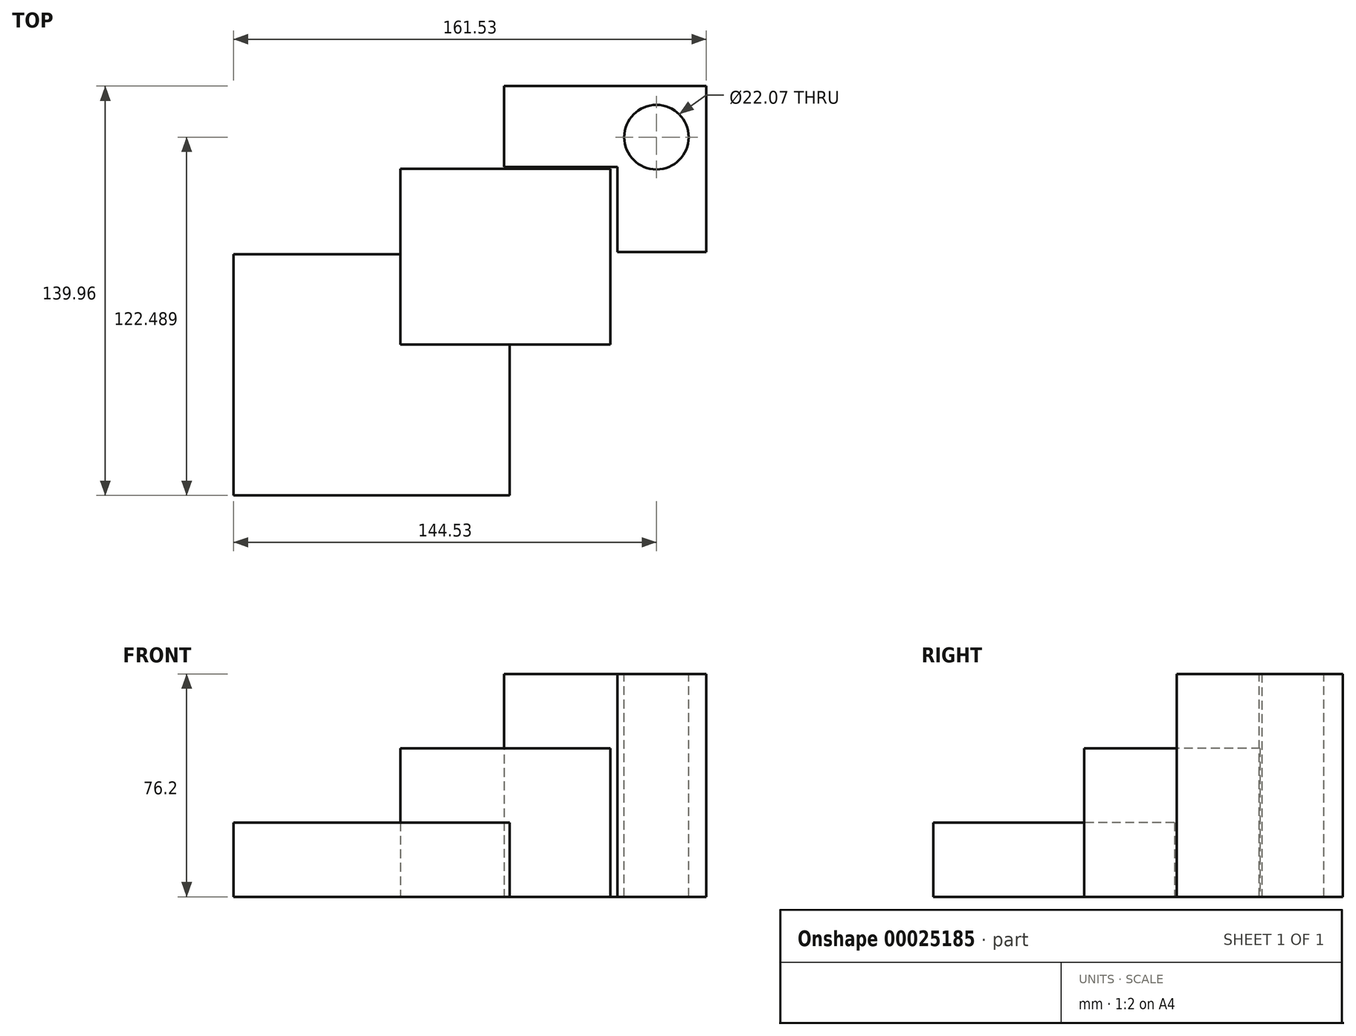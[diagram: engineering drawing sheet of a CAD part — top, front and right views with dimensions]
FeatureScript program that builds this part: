
annotation { "Feature Type Name" : "Feature", "Feature Type Description" : "" }
export const myFeature = defineFeature(function(context is Context, id is Id, definition is map)
    precondition{}
    {
        {
            var Q0;
            Q0=qCreatedBy(makeId("Top.planeOp"),FACE);
            var sketch = newSketch(context, id + "F0", { "sketchPlane" : qUnion([Q0])});
            skLineSegment(sketch, "E0.rect.bottom", {"start": v(75.23, 74.72) * mm, "end": v(6.16, 74.72) * mm});
            skLineSegment(sketch, "E0.rect.top", {"start": v(75.23, 18.03) * mm, "end": v(6.16, 18.03) * mm});
            skLineSegment(sketch, "E0.rect.left", {"start": v(75.23, 74.72) * mm, "end": v(75.23, 18.03) * mm});
            skLineSegment(sketch, "E0.rect.right", {"start": v(6.16, 74.72) * mm, "end": v(6.16, 18.03) * mm});
            skPoint(sketch, "E0.rect.middle", {"position": v(40.7, 46.37) * mm});
            skLineSegment(sketch, "E1.rect.bottom", {"start": v(-32.54, 47.05) * mm, "end": v(44.86, 47.05) * mm});
            skLineSegment(sketch, "E1.rect.top", {"start": v(-32.54, -10.99) * mm, "end": v(44.86, -10.99) * mm});
            skLineSegment(sketch, "E1.rect.left", {"start": v(-32.54, 47.05) * mm, "end": v(-32.54, -10.99) * mm});
            skLineSegment(sketch, "E1.rect.right", {"start": v(44.86, 47.05) * mm, "end": v(44.86, -10.99) * mm});
            skPoint(sketch, "E1.rect.middle", {"position": v(6.16, 18.03) * mm});
            skSolve(sketch);
        }
        {
            var Q0;
            {var subQ7=sQuery(id+"F0.wireOp",EDGE,"E0.rect.bottom");Q0=makeQuery(id+"F0.imprint","IMPRINT",FACE,{"disambiguationData":[TD([[makeQuery(id+"F0.imprint","IMPRINT",EDGE,{"derivedFrom":subQ7}),1.0]])]});}
            extrude(context, id + "F1", {"entities" : qUnion([Q0]), "depth" : 76.2 * mm});
        }
        {
            var Q0;
            Q0=qCreatedBy(makeId("Top.planeOp"),FACE);
            var sketch = newSketch(context, id + "F2", { "sketchPlane" : qUnion([Q0])});
            skLineSegment(sketch, "E2.rect.bottom", {"start": v(42.5, 46.48) * mm, "end": v(-29.26, 46.48) * mm});
            skLineSegment(sketch, "E2.rect.top", {"start": v(42.5, -13.62) * mm, "end": v(-29.26, -13.62) * mm});
            skLineSegment(sketch, "E2.rect.left", {"start": v(42.5, 46.48) * mm, "end": v(42.5, -13.62) * mm});
            skLineSegment(sketch, "E2.rect.right", {"start": v(-29.26, 46.48) * mm, "end": v(-29.26, -13.62) * mm});
            skPoint(sketch, "E2.rect.middle", {"position": v(6.62, 16.43) * mm});
            skSolve(sketch);
        }
        {
            var Q0;
            Q0=makeQuery(id+"F2.imprint","IMPRINT",FACE,{"disambiguationData":[TD([[makeQuery(id+"F2.imprint","IMPRINT",EDGE,{"derivedFrom":sQuery(id+"F2.wireOp",EDGE,"E2.rect.bottom")}),1.0]])]});
            extrude(context, id + "F3", {"entities" : qUnion([Q0]), "depth" : 50.8 * mm});
        }
        {
            var Q0;
            Q0=qCreatedBy(makeId("Top.planeOp"),FACE);
            var sketch = newSketch(context, id + "F4", { "sketchPlane" : qUnion([Q0])});
            skLineSegment(sketch, "E3.rect.bottom", {"start": v(8.02, 17.24) * mm, "end": v(-86.3, 17.24) * mm});
            skLineSegment(sketch, "E3.rect.top", {"start": v(8.02, -65.24) * mm, "end": v(-86.3, -65.24) * mm});
            skLineSegment(sketch, "E3.rect.left", {"start": v(8.02, 17.24) * mm, "end": v(8.02, -65.24) * mm});
            skLineSegment(sketch, "E3.rect.right", {"start": v(-86.3, 17.24) * mm, "end": v(-86.3, -65.24) * mm});
            skPoint(sketch, "E3.rect.middle", {"position": v(-39.14, -24) * mm});
            skSolve(sketch);
        }
        {
            var Q0;
            Q0=makeQuery(id+"F4.imprint","IMPRINT",FACE,{"disambiguationData":[TD([[makeQuery(id+"F4.imprint","IMPRINT",EDGE,{"derivedFrom":sQuery(id+"F4.wireOp",EDGE,"E3.rect.bottom")}),1.0]])]});
            extrude(context, id + "F5", {"entities" : qUnion([Q0]), "operationType" : NewBodyOperationType.ADD, "depth" : 25.4 * mm});
        }
        {
            var Q0;
            Q0=makeQuery(id+"F1.opExtrude","CAP_FACE",FACE,{"disambiguationData":[OSD([sQuery(id+"F0.wireOp",EDGE,"E0.rect.bottom"),sQuery(id+"F0.wireOp",EDGE,"E0.rect.top"),sQuery(id+"F0.wireOp",EDGE,"E0.rect.left"),sQuery(id+"F0.wireOp",EDGE,"E0.rect.right"),sQuery(id+"F0.wireOp",EDGE,"E1.rect.bottom"),sQuery(id+"F0.wireOp",EDGE,"E1.rect.right")])],"isStart":false});
            var sketch = newSketch(context, id + "F6", { "sketchPlane" : qUnion([Q0])});
            skCircle(sketch, "E4", {"center": v(58.23, 57.25) * mm, "radius": 11.04 * mm});
            skSolve(sketch);
        }
        {
            var Q0;
            Q0=makeQuery(id+"F6.imprint","IMPRINT",FACE,{"disambiguationData":[TD([[makeQuery(id+"F6.imprint","IMPRINT",EDGE,{"derivedFrom":sQuery(id+"F6.wireOp",EDGE,"E4")}),1.0]])]});
            extrude(context, id + "F7", {"entities" : qUnion([Q0]), "operationType" : NewBodyOperationType.REMOVE, "oppositeDirection" : true, "depth" : 101.6 * mm});
        }
    });
